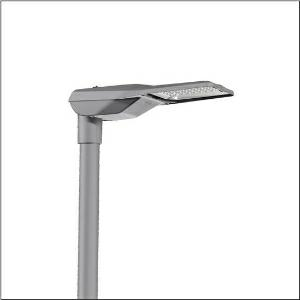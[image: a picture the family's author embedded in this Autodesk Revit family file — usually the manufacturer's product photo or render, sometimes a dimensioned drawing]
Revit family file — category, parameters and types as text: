
# Revit family: streetlight_sl_21_mini___stw1_0a_5xe2e43s08hb_ce20
name_source: partatom
category: Lighting Fixtures
units: mm (PartAtom-declared; Revit-internal decimal feet)

## family parameters
Cut with Voids When Loaded = No
Host = Face
Light Source = No
Part Type = Normal
Room Calculation Point = No
Round Connector Dimension = Use Diameter
Shared = No

## types (1)
- --- (1 x LED, 9430 lm, 66 W, 4000K)
    Apparent Load = 66 VA
    CIE Flux Codes = 38 75 98 100 100
    Color Rendering = 70
    Color Temperature = 4000K
    Default Elevation = 1800 mm
    Description = Streetlight SL 21 mini, mast luminaire, primary light control with lens, of PMMA, primary optical cover: cover, of toughened safety glass, transparent, light distribution: STW1.0a, light emission: direct distribution, primary light characteristic: asymmetric, installation type: side-entry, post-top, LED, High Power LED, rated luminous flux: 9.430lm, luminous efficacy: 143lm/W, light colour: 740, colour temperature: 4000K, control gear: D4i, control: overheat protection, constant luminous flux control, time-dependent luminous flux control, flexible luminous flux parameterisation, pre-setting: logarithmic dimming characteristic, mains connection: 220..240V, AC, 50/60Hz, start of lifetime: 66W, end of service life: 69W, reduction: 30W, luminaire housing, of diecast aluminium, powder-coated, SITECO metallic grey (DB 702S), corrosivity category C5 high according to DIN EN ISO 12944, please order mast flange separately, inclination adjustable: 0°, 5°, 10°, 15°, sealing non-destructively replaceable, multi-level sealing system, length: 628mm, width: 235mm, height: 110mm, mast flange for spigot size: 42mm (side-entry): 5XC10008XM4, 60/48mm (side-entry/post-top): 5XC10108XM2, 76/60mm (side-entry/post-top): 5XC10108XM1, mounting height: 4..8m, Smart Interface above, protection rating (complete): IP66, insulation class (complete): insulation class II (safety insulation), certification: CE, ENEC, ENEC+, VDE, impact resistance: IK10, permissible operating ambient temperature for outdoor applications: -40..+50°C, standard-compliant lighting for roads and squares, packaging unit: 1 piece

Light Distribution: STW1.0a
    Height = 110 mm
    Lamp = 1 x LED
    Lamp Light Flux = 9430 lm
    Lamp Power = 66 W
    Lamp count = 1
    Length = 625 mm
    Luminous efficacy = 143 lm/W
    Manufacturer = Siteco
    ModVariant = No
    Model = 5XE2E43S08HB
    Number of Poles = 1
    OnlyDefault = Yes
    Power Factor = 1
    Product Name = Streetlight SL 21 mini | STW1.0a
    Product group = mast luminaire | pylon top
    ProductGroupID = 6100
    Protection Class = Protection class II
    Protection Degree = IP 66
    RLX_Detail_Level = 1
    RLX_Emergency_Light_Flux = 0 lm
    RLX_Emergency_Type = 0
    RLX_Emergency_Type_DB = No
    RlxData = <blob elided: 26157 chars, md5=2793389b>
    Socket = socket
    Standby Power = 0 W
    System Light Flux = 9430 lm
    System Power = 66 W
    Type Comments = factory setting: luminous flux: 100 % | dim-lin: 254 | 670 mA
    Type Image = l_1003515.jpg
    URL = http://relux.com
    VarID = @adj_184799
    Voltage = 0 V
    Weight = 0.00 kg
    Width = 234 mm

## geometry (parser evidence)
native form markers: Blend x4, Sweep x12
no freeform markers — native parametric forms only
